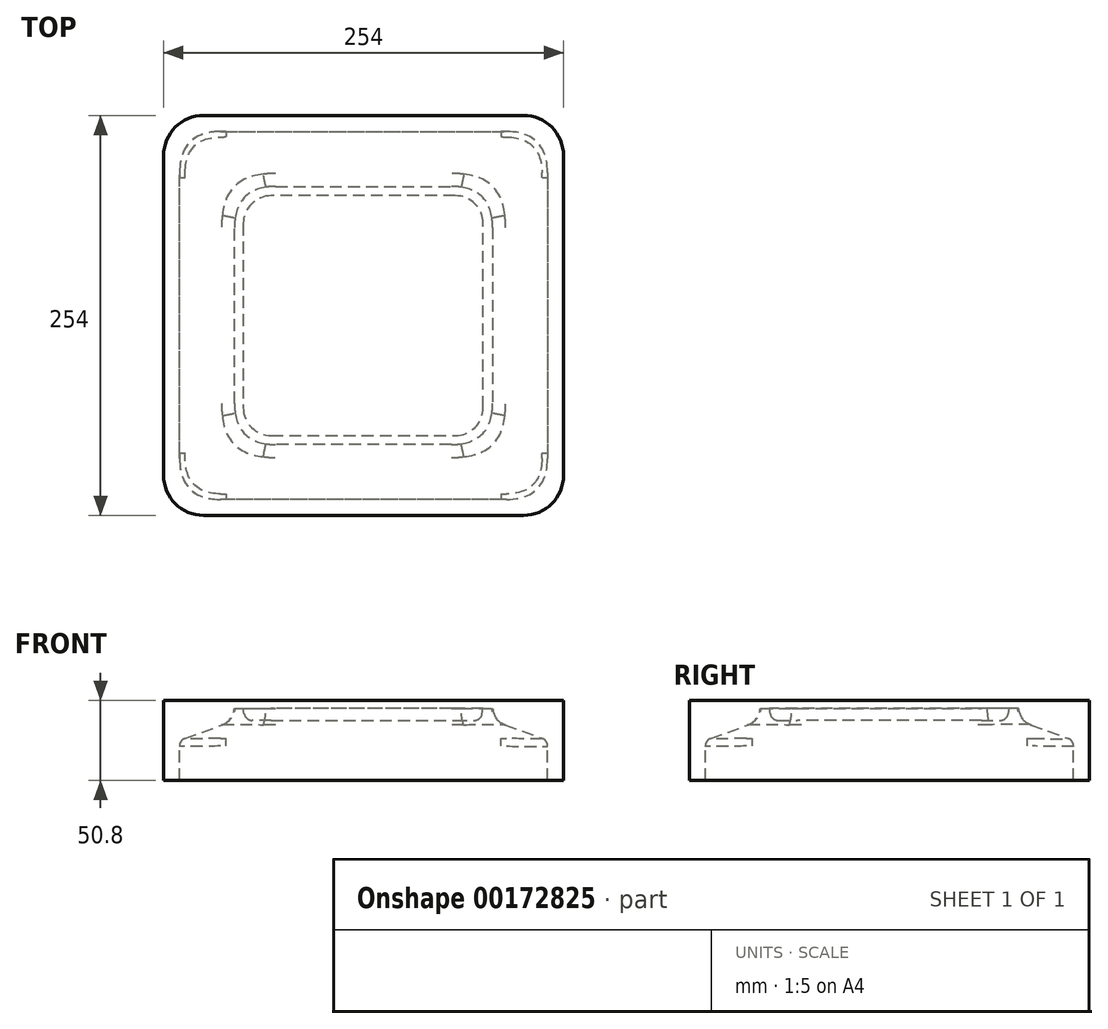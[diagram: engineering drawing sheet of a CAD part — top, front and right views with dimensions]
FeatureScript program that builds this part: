
annotation { "Feature Type Name" : "Feature", "Feature Type Description" : "" }
export const myFeature = defineFeature(function(context is Context, id is Id, definition is map)
    precondition{}
    {
        {
            var Q0;
            Q0=qCreatedBy(makeId("Top.planeOp"),FACE);
            var sketch = newSketch(context, id + "F0", { "sketchPlane" : qUnion([Q0])});
            skLineSegment(sketch, "E0.bottom", {"start": v(-0.04, 133.43) * mm, "end": v(203.16, 133.43) * mm});
            skLineSegment(sketch, "E0.top", {"start": v(-0.04, -120.57) * mm, "end": v(203.16, -120.57) * mm});
            skLineSegment(sketch, "E0.left", {"start": v(-25.44, 108.03) * mm, "end": v(-25.44, -95.17) * mm});
            skLineSegment(sketch, "E0.right", {"start": v(228.56, 108.03) * mm, "end": v(228.56, -95.17) * mm});
            skPoint(sketch, "E1.visualSharp", {"position": v(-25.44, -120.57) * mm});
            skArc(sketch, "E1.filletArc", {"start": v(-25.44, -95.17) * mm, "mid": v(-18, -113.13) * mm, "end": v(-0.04, -120.57) * mm});
            skPoint(sketch, "E2.visualSharp", {"position": v(228.56, -120.57) * mm});
            skArc(sketch, "E2.filletArc", {"start": v(203.16, -120.57) * mm, "mid": v(221.12, -113.13) * mm, "end": v(228.56, -95.17) * mm});
            skPoint(sketch, "E3.visualSharp", {"position": v(228.56, 133.43) * mm});
            skArc(sketch, "E3.filletArc", {"start": v(228.56, 108.03) * mm, "mid": v(221.12, 125.99) * mm, "end": v(203.16, 133.43) * mm});
            skPoint(sketch, "E4.visualSharp", {"position": v(-25.44, 133.43) * mm});
            skArc(sketch, "E4.filletArc", {"start": v(-0.04, 133.43) * mm, "mid": v(-18, 125.99) * mm, "end": v(-25.44, 108.03) * mm});
            skSolve(sketch);
        }
        {
            var Q0;
            Q0 = qSketchRegion(id + "F0", true);
            var Q1;
            Q1=sQuery(id+"F0.wireOp",EDGE,"E0.top");
            var Q2;
            Q2=sQuery(id+"F0.wireOp",EDGE,"E0.right");
            var Q3;
            Q3=sQuery(id+"F0.wireOp",EDGE,"E0.bottom");
            var Q4;
            Q4=sQuery(id+"F0.wireOp",EDGE,"E0.left");
            extrude(context, id + "F1", {"entities" : qUnion([Q0]), "surfaceEntities" : qUnion([Q1, Q2, Q3, Q4]), "depth" : 25.4 * mm});
        }
        {
            var Q0;
            Q0=qCreatedBy(makeId("Top.planeOp"),FACE);
            var sketch = newSketch(context, id + "F2", { "sketchPlane" : qUnion([Q0])});
            skLineSegment(sketch, "E5.bottom", {"start": v(5.04, -110.41) * mm, "end": v(198.08, -110.41) * mm});
            skLineSegment(sketch, "E5.top", {"start": v(5.04, 123.27) * mm, "end": v(198.08, 123.27) * mm});
            skLineSegment(sketch, "E5.left", {"start": v(-15.28, -90.1) * mm, "end": v(-15.28, 102.95) * mm});
            skLineSegment(sketch, "E5.right", {"start": v(218.4, -90.1) * mm, "end": v(218.4, 102.95) * mm});
            skPoint(sketch, "E6.visualSharp", {"position": v(-15.28, -110.41) * mm});
            skArc(sketch, "E6.filletArc", {"start": v(-15.28, -90.1) * mm, "mid": v(-9.33, -104.46) * mm, "end": v(5.04, -110.41) * mm});
            skPoint(sketch, "E7.visualSharp", {"position": v(-15.28, 123.27) * mm});
            skArc(sketch, "E7.filletArc", {"start": v(5.04, 123.27) * mm, "mid": v(-9.33, 117.32) * mm, "end": v(-15.28, 102.95) * mm});
            skPoint(sketch, "E8.visualSharp", {"position": v(218.4, 123.27) * mm});
            skArc(sketch, "E8.filletArc", {"start": v(218.4, 102.95) * mm, "mid": v(212.45, 117.32) * mm, "end": v(198.08, 123.27) * mm});
            skPoint(sketch, "E9.visualSharp", {"position": v(218.4, -110.41) * mm});
            skArc(sketch, "E9.filletArc", {"start": v(198.08, -110.41) * mm, "mid": v(212.45, -104.46) * mm, "end": v(218.4, -90.1) * mm});
            skSolve(sketch);
        }
        {
            var Q0;
            Q0=makeQuery(id+"F1.opExtrude","CAP_FACE",FACE,{"disambiguationData":[OSD([sQuery(id+"F0.wireOp",EDGE,"E0.bottom"),sQuery(id+"F0.wireOp",EDGE,"E0.top"),sQuery(id+"F0.wireOp",EDGE,"E0.left"),sQuery(id+"F0.wireOp",EDGE,"E0.right"),sQuery(id+"F0.wireOp",EDGE,"E1.filletArc"),sQuery(id+"F0.wireOp",EDGE,"E2.filletArc"),sQuery(id+"F0.wireOp",EDGE,"E3.filletArc"),sQuery(id+"F0.wireOp",EDGE,"E4.filletArc")])],"isStart":false});
            var sketch = newSketch(context, id + "F3", { "sketchPlane" : qUnion([Q0])});
            skLineSegment(sketch, "E10.bottom", {"start": v(0, 108.49) * mm, "end": v(203.2, 108.49) * mm});
            skLineSegment(sketch, "E10.top", {"start": v(0, -94.71) * mm, "end": v(203.2, -94.71) * mm});
            skLineSegment(sketch, "E10.left", {"start": v(0, 108.49) * mm, "end": v(0, -94.71) * mm});
            skLineSegment(sketch, "E10.right", {"start": v(203.2, 108.49) * mm, "end": v(203.2, -94.71) * mm});
            skSolve(sketch);
        }
        {
            var Q0;
            Q0 = qSketchRegion(id + "F3", true);
            extrude(context, id + "F4", {"entities" : qUnion([Q0]), "operationType" : NewBodyOperationType.ADD, "oppositeDirection" : true, "depth" : 25.4 * mm});
        }
        {
            var Q0;
            Q0 = qSketchRegion(id + "F2", true);
            extrude(context, id + "F5", {"entities" : qUnion([Q0]), "operationType" : NewBodyOperationType.REMOVE, "depth" : 12.7 * mm, "hasDraft" : true, "draftAngle" : 70 * degree, "draftPullDirection" : true});
        }
        {
            var Q0;
            {var subQ0=sQuery(id+"F2.wireOp",EDGE,"E8.filletArc");Q0=makeQuery(id+"F5.boolean.opBoolean","COPY",EDGE,{"derivedFrom":makeQuery(id+"F5.draft0.opDraft","MERGE",EDGE,{"derivedFrom":[makeQuery(id+"F5.opExtrude","SWEPT_EDGE",EDGE,{"disambiguationData":[OSD([sQuery(id+"F2.wireOp",EDGE,"E5.top"),subQ0])]}),makeQuery(id+"F5.opExtrude","SWEPT_EDGE",EDGE,{"disambiguationData":[OSD([sQuery(id+"F2.wireOp",EDGE,"E5.right"),subQ0])]})]})});}
            var Q1;
            {var subQ0=sQuery(id+"F2.wireOp",EDGE,"E7.filletArc");Q1=makeQuery(id+"F5.boolean.opBoolean","COPY",EDGE,{"derivedFrom":makeQuery(id+"F5.draft0.opDraft","MERGE",EDGE,{"derivedFrom":[makeQuery(id+"F5.opExtrude","SWEPT_EDGE",EDGE,{"disambiguationData":[OSD([sQuery(id+"F2.wireOp",EDGE,"E5.top"),subQ0])]}),makeQuery(id+"F5.opExtrude","SWEPT_EDGE",EDGE,{"disambiguationData":[OSD([sQuery(id+"F2.wireOp",EDGE,"E5.left"),subQ0])]})]})});}
            var Q2;
            {var subQ0=sQuery(id+"F2.wireOp",EDGE,"E6.filletArc");Q2=makeQuery(id+"F5.boolean.opBoolean","COPY",EDGE,{"derivedFrom":makeQuery(id+"F5.draft0.opDraft","MERGE",EDGE,{"derivedFrom":[makeQuery(id+"F5.opExtrude","SWEPT_EDGE",EDGE,{"disambiguationData":[OSD([sQuery(id+"F2.wireOp",EDGE,"E5.bottom"),subQ0])]}),makeQuery(id+"F5.opExtrude","SWEPT_EDGE",EDGE,{"disambiguationData":[OSD([sQuery(id+"F2.wireOp",EDGE,"E5.left"),subQ0])]})]})});}
            var Q3;
            {var subQ0=sQuery(id+"F2.wireOp",EDGE,"E9.filletArc");Q3=makeQuery(id+"F5.boolean.opBoolean","COPY",EDGE,{"derivedFrom":makeQuery(id+"F5.draft0.opDraft","MERGE",EDGE,{"derivedFrom":[makeQuery(id+"F5.opExtrude","SWEPT_EDGE",EDGE,{"disambiguationData":[OSD([sQuery(id+"F2.wireOp",EDGE,"E5.bottom"),subQ0])]}),makeQuery(id+"F5.opExtrude","SWEPT_EDGE",EDGE,{"disambiguationData":[OSD([sQuery(id+"F2.wireOp",EDGE,"E5.right"),subQ0])]})]})});}
            fillet(context, id + "F6", {"entities" : qUnion([Q0, Q1, Q2, Q3]), "radius" : 76.2 * mm, "tangentPropagation" : true, "allowEdgeOverflow" : false});
        }
        {
            var Q0;
            Q0=makeQuery(id+"F5.boolean.opBoolean","COPY",FACE,{"derivedFrom":makeQuery(id+"F5.opExtrude","CAP_FACE",FACE,{"disambiguationData":[OSD([sQuery(id+"F2.wireOp",EDGE,"E5.bottom"),sQuery(id+"F2.wireOp",EDGE,"E5.top"),sQuery(id+"F2.wireOp",EDGE,"E5.left"),sQuery(id+"F2.wireOp",EDGE,"E5.right"),sQuery(id+"F2.wireOp",EDGE,"E6.filletArc"),sQuery(id+"F2.wireOp",EDGE,"E7.filletArc"),sQuery(id+"F2.wireOp",EDGE,"E8.filletArc"),sQuery(id+"F2.wireOp",EDGE,"E9.filletArc")])],"isStart":false})});
            extrude(context, id + "F7", {"entities" : qUnion([Q0]), "operationType" : NewBodyOperationType.REMOVE, "oppositeDirection" : true, "depth" : 7.62 * mm});
        }
        {
            var Q0;
            {var subQ0=sQuery(id+"F2.wireOp",EDGE,"E5.top");Q0=makeQuery(id+"F7.boolean.opBoolean","MERGE",EDGE,{"derivedFrom":[makeQuery(id+"F5.boolean.opBoolean","COPY",EDGE,{"derivedFrom":makeQuery(id+"F5.opExtrude","CAP_EDGE",EDGE,{"disambiguationData":[OSD([subQ0])],"isStart":false})}),makeQuery(id+"F7.opExtrude","CAP_EDGE",EDGE,{"disambiguationData":[OSD([subQ0])],"isStart":true})]});}
            fillet(context, id + "F8", {"entities" : qUnion([Q0]), "radius" : 12.7 * mm, "tangentPropagation" : true, "allowEdgeOverflow" : false});
        }
        {
            var Q0;
            Q0=makeQuery(id+"F1.opExtrude","CAP_FACE",FACE,{"disambiguationData":[OSD([sQuery(id+"F0.wireOp",EDGE,"E0.bottom"),sQuery(id+"F0.wireOp",EDGE,"E0.top"),sQuery(id+"F0.wireOp",EDGE,"E0.left"),sQuery(id+"F0.wireOp",EDGE,"E0.right"),sQuery(id+"F0.wireOp",EDGE,"E1.filletArc"),sQuery(id+"F0.wireOp",EDGE,"E2.filletArc"),sQuery(id+"F0.wireOp",EDGE,"E3.filletArc"),sQuery(id+"F0.wireOp",EDGE,"E4.filletArc")])],"isStart":true});
            extrude(context, id + "F9", {"entities" : qUnion([Q0]), "operationType" : NewBodyOperationType.ADD, "depth" : 25.4 * mm});
        }
        {
            var Q0;
            {var subQ0=sQuery(id+"F2.wireOp",EDGE,"E5.bottom");Q0=makeQuery(id+"F9.boolean.opBoolean","MERGE",EDGE,{"derivedFrom":[makeQuery(id+"F5.boolean.opBoolean","COPY",EDGE,{"derivedFrom":makeQuery(id+"F5.opExtrude","CAP_EDGE",EDGE,{"disambiguationData":[OSD([subQ0])],"isStart":true})}),makeQuery(id+"F9.opExtrude","CAP_EDGE",EDGE,{"disambiguationData":[OSD([subQ0])],"isStart":true})]});}
            fillet(context, id + "F10", {"entities" : qUnion([Q0]), "radius" : 5.08 * mm, "tangentPropagation" : true, "allowEdgeOverflow" : false});
        }
        {
            var Q0;
            Q0=makeQuery(id+"F7.boolean.opBoolean","COPY",FACE,{"derivedFrom":makeQuery(id+"F7.opExtrude","CAP_FACE",FACE,{"disambiguationData":[OSD([sQuery(id+"F2.wireOp",EDGE,"E5.bottom"),sQuery(id+"F2.wireOp",EDGE,"E5.top"),sQuery(id+"F2.wireOp",EDGE,"E5.left"),sQuery(id+"F2.wireOp",EDGE,"E5.right"),sQuery(id+"F2.wireOp",EDGE,"E6.filletArc"),sQuery(id+"F2.wireOp",EDGE,"E7.filletArc"),sQuery(id+"F2.wireOp",EDGE,"E8.filletArc"),sQuery(id+"F2.wireOp",EDGE,"E9.filletArc")])],"isStart":false})});
            var sketch = newSketch(context, id + "F11", { "sketchPlane" : qUnion([Q0])});
            skLineSegment(sketch, "E11.bottom", {"start": v(42.93, 69.88) * mm, "end": v(159.77, 69.88) * mm});
            skLineSegment(sketch, "E11.top", {"start": v(42.93, -82.52) * mm, "end": v(159.77, -82.52) * mm});
            skLineSegment(sketch, "E11.left", {"start": v(25.15, 52.1) * mm, "end": v(25.15, -64.74) * mm});
            skLineSegment(sketch, "E11.right", {"start": v(177.55, 52.1) * mm, "end": v(177.55, -64.74) * mm});
            skPoint(sketch, "E12.visualSharp", {"position": v(25.15, 69.88) * mm});
            skArc(sketch, "E12.filletArc", {"start": v(42.93, 69.88) * mm, "mid": v(30.36, 64.68) * mm, "end": v(25.15, 52.1) * mm});
            skPoint(sketch, "E13.visualSharp", {"position": v(177.55, 69.88) * mm});
            skArc(sketch, "E13.filletArc", {"start": v(177.55, 52.1) * mm, "mid": v(172.35, 64.68) * mm, "end": v(159.77, 69.88) * mm});
            skPoint(sketch, "E14.visualSharp", {"position": v(177.55, -82.52) * mm});
            skArc(sketch, "E14.filletArc", {"start": v(159.77, -82.52) * mm, "mid": v(172.35, -77.3) * mm, "end": v(177.55, -64.74) * mm});
            skPoint(sketch, "E15.visualSharp", {"position": v(25.15, -82.52) * mm});
            skArc(sketch, "E15.filletArc", {"start": v(25.15, -64.74) * mm, "mid": v(30.36, -77.3) * mm, "end": v(42.93, -82.52) * mm});
            skSolve(sketch);
        }
        {
            var Q0;
            Q0 = qSketchRegion(id + "F11", true);
            extrude(context, id + "F12", {"entities" : qUnion([Q0]), "operationType" : NewBodyOperationType.ADD, "depth" : 7.62 * mm, "hasDraft" : true, "draftAngle" : 10 * degree, "draftPullDirection" : true});
        }
        {
            var Q0;
            Q0=makeQuery(id+"F12.opExtrude","CAP_EDGE",EDGE,{"disambiguationData":[OSD([sQuery(id+"F11.wireOp",EDGE,"E11.left")])],"isStart":false});
            fillet(context, id + "F13", {"entities" : qUnion([Q0]), "radius" : 5.08 * mm, "tangentPropagation" : true, "allowEdgeOverflow" : false});
        }
    });
